# Revit family: NBS_HeatraeSadia_StrgWtrHtrsElctrc_Supreme
name_source: partatom
category: Plumbing Fixtures
revit_build: Autodesk Revit 2014 (Build: 20130709_2115(x64)
units: mm (PartAtom-declared; Revit-internal decimal feet)

## types (3) — shared parameters
Arrangement = Single point – mains supply
AssetType = Fixed
CW Connection = Yes
CasingFinish = White thermoplastic
Color = Natural
Connections = Bottom or rear entry is possible using 15 mm push-fit connections
Controls = White push/ pull lever
Description = Water boiling heater
DurationUnit = year
Features = Intelliboil™Plus technology, integral electronic water conditioner, power 'on’ indicator, ‘ready’ indicator, detachable steam condensing chamber
Fixing = Wall fixed
FlowRate = To suit draw off requirements
HW Connection = Yes
HeatTransferSurfaceArea = 0
IPCode = IPX2
IfcExportAs = IfcBoilerType
IfcExportType = WATER
IsWaterStorageHeater = Yes
ManufacturerName = Heatrae Sadia
ManufacturerURL = www.heatraesadia.com
Material = Outer casing: High impact thermoplastic; Water container: Moulded polyphenylene sulphide; Heat unit: Low watt density Superloy element
NBSCertification = http://www.nationalbimlibrary.com
NBSDescription = Storage water heaters, electric
NBSReference = 90-15-35/440
OutletTemperatureRange = 100
PartialLoadEfficiencyCurves = 0
PressureRating = 0
ProductInformation = www.heatraesadia.com/docs/Drinking_water_brochure.pdf
Rating = 2.5 kW
SafetyFeatures = Low pressure vented, dry start protection by self-resetting bi-metal thermal cut-out, boil-dry protection by manually-resettable disc-type bi-metal cut-out
StorageWaterHeaterMaterial = NBS_Concept
ThermalInsulation = CFC/HCFC free (ODP zero) pre-moulded polystyrene and thermoplastic blend
ThirdPartyCertification = BEAB approved
Uniclass2 = 90-90-46/428
Uniclass2015Description = Electric storage water heaters
Uniclass2015Reference = Pr_60_60_96_28
Uniclass2015Version = Products v1.1
Vent Connection = Yes
Version = 1
WarrantyDurationParts = 2
WarrantyDurationUnit = year
WarrantyStartDate = 1900-12-31T23:59:59
Waste Connection = No
WaterInletTemperatureRange = 0
zero-valued in all types: HeatOutput, NominalEfficiency, NominalEnergyConsumption, NominalPartLoadRatio

## per-type parameters (varying)
| type | Accessories | BIMObjectName | Depth | Height | ModelNumber | ModelReference | Name | NominalHeight | NominalLength | NominalWidth | Size | WaterStorageCapacity | Weight | Width |
| Supreme150 | Counter stand (95:970:132), Drip tray no waste (95:970:128), Drip tray with waste (95:970:123), Programmable timer (95:970:124), Water filter system (95:970:129) | NBS_HeatraeSadia_StorageWaterHeatersElectric_Supreme150 | 190 mm | 445 mm  [stored 1.45997 ft] | 95:200:252 | Supreme 150 | StorageWaterHeatersElectric_Supreme150_HeatraeSadia | 445 mm  [stored 1.45997 ft] | 190 mm | 290 mm  [stored 0.951444 ft] | 445 x 290 x 190 mm | 2.5 | 8.4 | 290 mm  [stored 0.951444 ft] |
| Supreme165 | Counter stand (95:970:133), Drip tray no waste (95:970:128), Drip tray with waste (95:970:123), Programmable timer (95:970:124), Water filter system (95:970:129) | NBS_HeatraeSadia_StorageWaterHeatersElectric_Supreme165 | 200 mm  [stored 0.656168 ft] | 510 mm  [stored 1.67323 ft] | 95:200:253 | Supreme 165 | StorageWaterHeatersElectric_Supreme165_HeatraeSadia | 510 mm  [stored 1.67323 ft] | 200 mm  [stored 0.656168 ft] | 335 mm  [stored 1.09908 ft] | 510 x 335 x 200 mm | 5 | 11.8 | 335 mm  [stored 1.09908 ft] |
| Supreme180 | Counter stand (95:970:133), Drip tray no waste (95:970:128), Drip tray with waste (95:970:123), Programmable timer (95:970:124), Water filter system (95:970:129) | NBS_HeatraeSadia_StorageWaterHeatersElectric_Supreme180 | 262 mm  [stored 0.85958 ft] | 510 mm  [stored 1.67323 ft] | 95:200:254 | Supreme 180 | StorageWaterHeatersElectric_Supreme180_HeatraeSadia | 510 mm  [stored 1.67323 ft] | 262 mm  [stored 0.85958 ft] | 335 mm  [stored 1.09908 ft] | 510 x 335 x 262 mm | 7.5 | 15.4 | 335 mm  [stored 1.09908 ft] |

note: [stored X ft] marks values corroborated as IEEE doubles in the binary element streams (Revit-internal decimal feet)

## geometry (parser evidence)
native form markers: Blend x13, Sweep x1
no freeform markers — native parametric forms only
